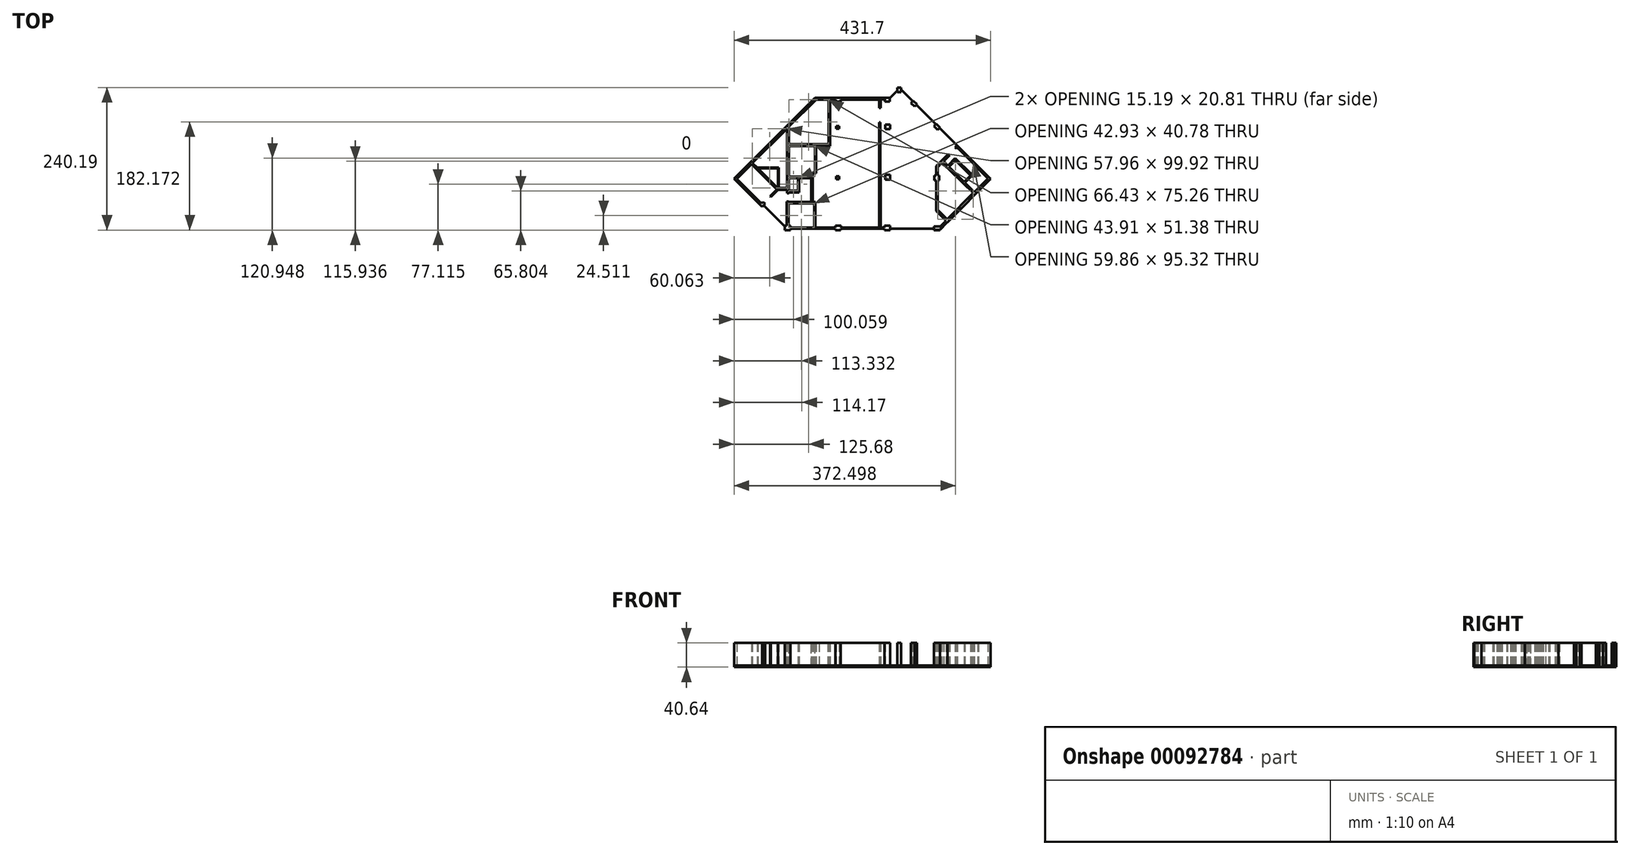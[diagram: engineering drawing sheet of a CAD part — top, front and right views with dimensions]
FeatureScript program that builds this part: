
annotation { "Feature Type Name" : "Feature", "Feature Type Description" : "" }
export const myFeature = defineFeature(function(context is Context, id is Id, definition is map)
    precondition{}
    {
        {
            var Q0;
            Q0=qCreatedBy(makeId("Top.planeOp"),FACE);
            var sketch = newSketch(context, id + "F0", { "sketchPlane" : qUnion([Q0])});
            skLineSegment(sketch, "E0", {"start": v(-79.76, 102.69) * mm, "end": v(-215.75, -33.59) * mm});
            skLineSegment(sketch, "E1", {"start": v(-215.75, -33.59) * mm, "end": v(-168.57, -80.77) * mm});
            skLineSegment(sketch, "E2", {"start": v(-168.57, -80.77) * mm, "end": v(-163.72, -75.92) * mm});
            skLineSegment(sketch, "E3", {"start": v(-163.72, -75.92) * mm, "end": v(-167.29, -72.36) * mm});
            skLineSegment(sketch, "E4", {"start": v(-167.29, -72.36) * mm, "end": v(-169.85, -74.93) * mm});
            skLineSegment(sketch, "E5", {"start": v(-169.85, -74.93) * mm, "end": v(-211.2, -33.59) * mm});
            skLineSegment(sketch, "E6", {"start": v(-211.2, -33.59) * mm, "end": v(-186.4, -8.8) * mm});
            skLineSegment(sketch, "E7", {"start": v(-186.4, -8.8) * mm, "end": v(-143.7, -51.47) * mm});
            skLineSegment(sketch, "E8", {"start": v(-143.7, -51.47) * mm, "end": v(-155.43, -62.87) * mm});
            skLineSegment(sketch, "E9", {"start": v(-155.43, -62.87) * mm, "end": v(-153.86, -64.43) * mm});
            skLineSegment(sketch, "E10", {"start": v(-153.86, -64.43) * mm, "end": v(-141.88, -52.4) * mm});
            skLineSegment(sketch, "E11", {"start": v(-141.88, -52.4) * mm, "end": v(-126.8, -52.4) * mm});
            skLineSegment(sketch, "E12", {"start": v(-126.8, -52.4) * mm, "end": v(-126.8, -58.13) * mm});
            skLineSegment(sketch, "E13", {"start": v(-126.8, -58.13) * mm, "end": v(-123.38, -58.13) * mm});
            skLineSegment(sketch, "E14", {"start": v(-123.38, -58.13) * mm, "end": v(-123.38, -56.96) * mm});
            skLineSegment(sketch, "E15", {"start": v(-123.38, -56.96) * mm, "end": v(-106.13, -56.96) * mm});
            skLineSegment(sketch, "E16", {"start": v(-106.13, -56.96) * mm, "end": v(-106.13, -50.83) * mm});
            skLineSegment(sketch, "E17", {"start": v(-106.13, -50.83) * mm, "end": v(-106.13, -40.44) * mm});
            skLineSegment(sketch, "E18", {"start": v(-106.13, -40.44) * mm, "end": v(-106.13, -32.6) * mm});
            skLineSegment(sketch, "E19", {"start": v(-106.13, -32.6) * mm, "end": v(-104.14, -32.6) * mm});
            skLineSegment(sketch, "E20", {"start": v(-104.14, -32.6) * mm, "end": v(-86.11, -32.44) * mm});
            skLineSegment(sketch, "E21", {"start": v(-86.11, -32.44) * mm, "end": v(-86.08, -56.63) * mm});
            skLineSegment(sketch, "E22", {"start": v(-86.08, -56.63) * mm, "end": v(-86.18, -72.93) * mm});
            skLineSegment(sketch, "E23", {"start": v(-86.18, -72.93) * mm, "end": v(-123.98, -72.93) * mm});
            skLineSegment(sketch, "E24", {"start": v(-123.98, -72.93) * mm, "end": v(-123.98, -71.84) * mm});
            skLineSegment(sketch, "E25", {"start": v(-123.98, -71.84) * mm, "end": v(-127, -71.84) * mm});
            skLineSegment(sketch, "E26", {"start": v(-127, -71.84) * mm, "end": v(-127, -112.56) * mm});
            skLineSegment(sketch, "E27", {"start": v(-127, -112.56) * mm, "end": v(-130.71, -112.56) * mm});
            skLineSegment(sketch, "E28", {"start": v(-130.71, -112.56) * mm, "end": v(-130.71, -120.1) * mm});
            skLineSegment(sketch, "E29", {"start": v(-130.71, -120.1) * mm, "end": v(-121.24, -120.1) * mm});
            skLineSegment(sketch, "E30", {"start": v(-121.24, -120.1) * mm, "end": v(-121.24, -117.8) * mm});
            skLineSegment(sketch, "E31", {"start": v(-121.24, -117.8) * mm, "end": v(-45.65, -117.8) * mm});
            skLineSegment(sketch, "E32", {"start": v(-45.65, -117.8) * mm, "end": v(-45.65, -120.1) * mm});
            skLineSegment(sketch, "E33", {"start": v(-45.65, -120.1) * mm, "end": v(-36.17, -120.1) * mm});
            skLineSegment(sketch, "E34", {"start": v(-36.17, -120.1) * mm, "end": v(-36.17, -117.8) * mm});
            skLineSegment(sketch, "E35", {"start": v(-36.17, -117.8) * mm, "end": v(30.57, -117.8) * mm});
            skLineSegment(sketch, "E36", {"start": v(30.57, -117.8) * mm, "end": v(30.57, -117.83) * mm});
            skLineSegment(sketch, "E37", {"start": v(30.57, -117.83) * mm, "end": v(37.4, -117.82) * mm});
            skLineSegment(sketch, "E38", {"start": v(37.4, -117.82) * mm, "end": v(37.4, -120.1) * mm});
            skLineSegment(sketch, "E39", {"start": v(37.4, -120.1) * mm, "end": v(46.88, -120.1) * mm});
            skLineSegment(sketch, "E40", {"start": v(46.88, -120.1) * mm, "end": v(46.88, -112.56) * mm});
            skLineSegment(sketch, "E41", {"start": v(46.88, -112.56) * mm, "end": v(37.4, -112.56) * mm});
            skLineSegment(sketch, "E42", {"start": v(37.4, -112.56) * mm, "end": v(37.4, -115.98) * mm});
            skLineSegment(sketch, "E43", {"start": v(37.4, -115.98) * mm, "end": v(30.64, -115.98) * mm});
            skLineSegment(sketch, "E44", {"start": v(30.64, -115.98) * mm, "end": v(30.28, 61.63) * mm});
            skLineSegment(sketch, "E45", {"start": v(30.28, 61.63) * mm, "end": v(28, 61.63) * mm});
            skLineSegment(sketch, "E46", {"start": v(28, 61.63) * mm, "end": v(28, -115.99) * mm});
            skLineSegment(sketch, "E47", {"start": v(28, -115.99) * mm, "end": v(-36.17, -115.99) * mm});
            skLineSegment(sketch, "E48", {"start": v(-36.17, -115.99) * mm, "end": v(-36.17, -112.56) * mm});
            skLineSegment(sketch, "E49", {"start": v(-36.17, -112.56) * mm, "end": v(-45.65, -112.56) * mm});
            skLineSegment(sketch, "E50", {"start": v(-45.65, -112.56) * mm, "end": v(-45.65, -115.99) * mm});
            skLineSegment(sketch, "E51", {"start": v(-45.65, -115.99) * mm, "end": v(-78.77, -115.99) * mm});
            skLineSegment(sketch, "E52", {"start": v(-78.77, -115.99) * mm, "end": v(-78.77, -72.93) * mm});
            skLineSegment(sketch, "E53", {"start": v(-78.77, -72.93) * mm, "end": v(-83.56, -72.93) * mm});
            skLineSegment(sketch, "E54", {"start": v(-83.56, -72.93) * mm, "end": v(-83.56, -58.24) * mm});
            skLineSegment(sketch, "E55", {"start": v(-83.56, -58.24) * mm, "end": v(-83.56, -24.67) * mm});
            skLineSegment(sketch, "E56", {"start": v(-83.56, -24.67) * mm, "end": v(-77.61, -24.67) * mm});
            skLineSegment(sketch, "E57", {"start": v(-77.61, -24.67) * mm, "end": v(-77.61, 21.4) * mm});
            skLineSegment(sketch, "E58", {"start": v(-77.61, 21.4) * mm, "end": v(-59.24, 21.44) * mm});
            skLineSegment(sketch, "E59", {"start": v(-59.24, 21.44) * mm, "end": v(-54.1, 21.44) * mm});
            skLineSegment(sketch, "E60", {"start": v(-54.1, 21.44) * mm, "end": v(-54.1, 99.7) * mm});
            skLineSegment(sketch, "E61", {"start": v(-54.1, 99.7) * mm, "end": v(-44.98, 99.7) * mm});
            skLineSegment(sketch, "E62", {"start": v(-44.98, 99.7) * mm, "end": v(-44.98, 96.56) * mm});
            skLineSegment(sketch, "E63", {"start": v(-44.98, 96.56) * mm, "end": v(-36.57, 96.56) * mm});
            skLineSegment(sketch, "E64", {"start": v(-36.57, 96.56) * mm, "end": v(-36.57, 99.7) * mm});
            skLineSegment(sketch, "E65", {"start": v(-36.57, 99.7) * mm, "end": v(28.57, 99.7) * mm});
            skLineSegment(sketch, "E66", {"start": v(28.57, 99.7) * mm, "end": v(28.57, 85.58) * mm});
            skLineSegment(sketch, "E67", {"start": v(28.57, 85.58) * mm, "end": v(30.91, 85.64) * mm});
            skLineSegment(sketch, "E68", {"start": v(30.91, 85.64) * mm, "end": v(30.91, 100.4) * mm});
            skLineSegment(sketch, "E69", {"start": v(30.91, 100.4) * mm, "end": v(37.7, 100.4) * mm});
            skLineSegment(sketch, "E70", {"start": v(37.7, 100.4) * mm, "end": v(37.7, 96.56) * mm});
            skLineSegment(sketch, "E71", {"start": v(37.7, 96.56) * mm, "end": v(46.1, 96.56) * mm});
            skLineSegment(sketch, "E72", {"start": v(46.1, 96.56) * mm, "end": v(46.1, 102.4) * mm});
            skLineSegment(sketch, "E73", {"start": v(46.1, 102.4) * mm, "end": v(37.73, 102.4) * mm});
            skLineSegment(sketch, "E74", {"start": v(37.73, 102.4) * mm, "end": v(37.7, 102.69) * mm});
            skLineSegment(sketch, "E75", {"start": v(37.7, 102.69) * mm, "end": v(-79.76, 102.69) * mm});
            skLineSegment(sketch, "E76", {"start": v(-77.91, 99.7) * mm, "end": v(-56.96, 99.7) * mm});
            skLineSegment(sketch, "E77", {"start": v(-56.96, 99.7) * mm, "end": v(-56.96, 24.5) * mm});
            skLineSegment(sketch, "E78", {"start": v(-56.96, 24.5) * mm, "end": v(-58.2, 24.43) * mm});
            skLineSegment(sketch, "E79", {"start": v(-58.2, 24.43) * mm, "end": v(-72.92, 24.58) * mm});
            skLineSegment(sketch, "E80", {"start": v(-72.92, 24.58) * mm, "end": v(-123.38, 24.47) * mm});
            skLineSegment(sketch, "E81", {"start": v(-123.38, 24.47) * mm, "end": v(-123.38, 54.22) * mm});
            skLineSegment(sketch, "E82", {"start": v(-123.38, 54.22) * mm, "end": v(-77.91, 99.7) * mm});
            skFitSpline(sketch, "E83", {"points": [v(-79.84, 21.43) * mm, v(-80.03, 20.07) * mm, v(-79.83, -23.46) * mm, v(-79.83, -23.46) * mm, v(-79.84, 21.43) * mm]});
            skLineSegment(sketch, "E84", {"start": v(-126.8, 50.8) * mm, "end": v(-126.8, -49.12) * mm});
            skLineSegment(sketch, "E85", {"start": v(-126.8, -49.12) * mm, "end": v(-140.51, -49.12) * mm});
            skLineSegment(sketch, "E86", {"start": v(-140.51, -49.12) * mm, "end": v(-140.51, -14.9) * mm});
            skLineSegment(sketch, "E87", {"start": v(-140.51, -14.9) * mm, "end": v(-177.03, -14.9) * mm});
            skLineSegment(sketch, "E88", {"start": v(-177.03, -14.9) * mm, "end": v(-184.77, -7.17) * mm});
            skLineSegment(sketch, "E89", {"start": v(-184.77, -7.17) * mm, "end": v(-126.8, 50.8) * mm});
            skLineSegment(sketch, "E90", {"start": v(-79.83, -23.46) * mm, "end": v(-85.98, -23.46) * mm});
            skLineSegment(sketch, "E91", {"start": v(-85.98, -23.46) * mm, "end": v(-85.98, -29.82) * mm});
            skLineSegment(sketch, "E92", {"start": v(-85.98, -29.82) * mm, "end": v(-88.67, -29.8) * mm});
            skLineSegment(sketch, "E93", {"start": v(-88.67, -29.8) * mm, "end": v(-93, -29.84) * mm});
            skLineSegment(sketch, "E94", {"start": v(-93, -29.84) * mm, "end": v(-100.1, -29.88) * mm});
            skLineSegment(sketch, "E95", {"start": v(-100.1, -29.88) * mm, "end": v(-103.14, -29.88) * mm});
            skLineSegment(sketch, "E96", {"start": v(-103.14, -29.88) * mm, "end": v(-123.38, -29.88) * mm});
            skLineSegment(sketch, "E97", {"start": v(-123.38, -29.88) * mm, "end": v(-123.38, 21.34) * mm});
            skLineSegment(sketch, "E98", {"start": v(-123.38, 21.34) * mm, "end": v(-79.84, 21.43) * mm});
            skLineSegment(sketch, "E99", {"start": v(-175.82, -16.1) * mm, "end": v(-141.82, -16.1) * mm});
            skLineSegment(sketch, "E100", {"start": v(-141.82, -16.1) * mm, "end": v(-141.82, -49.12) * mm});
            skLineSegment(sketch, "E101", {"start": v(-141.82, -49.12) * mm, "end": v(-142.77, -49.12) * mm});
            skLineSegment(sketch, "E102", {"start": v(-142.77, -49.12) * mm, "end": v(-175.82, -16.1) * mm});
            skLineSegment(sketch, "E103", {"start": v(-123.38, -32.6) * mm, "end": v(-108.2, -32.6) * mm});
            skLineSegment(sketch, "E104", {"start": v(-108.2, -32.6) * mm, "end": v(-108.2, -39.52) * mm});
            skLineSegment(sketch, "E105", {"start": v(-108.2, -39.52) * mm, "end": v(-108.4, -50.63) * mm});
            skLineSegment(sketch, "E106", {"start": v(-108.4, -50.63) * mm, "end": v(-108.38, -53.4) * mm});
            skLineSegment(sketch, "E107", {"start": v(-108.38, -53.4) * mm, "end": v(-123.38, -53.4) * mm});
            skLineSegment(sketch, "E108", {"start": v(-123.38, -53.4) * mm, "end": v(-123.38, -32.6) * mm});
            skLineSegment(sketch, "E109", {"start": v(-123.98, -75.2) * mm, "end": v(-81.05, -75.2) * mm});
            skLineSegment(sketch, "E110", {"start": v(-81.05, -75.2) * mm, "end": v(-81.05, -115.98) * mm});
            skLineSegment(sketch, "E111", {"start": v(-81.05, -115.98) * mm, "end": v(-121.24, -115.99) * mm});
            skLineSegment(sketch, "E112", {"start": v(-121.24, -115.99) * mm, "end": v(-121.24, -112.56) * mm});
            skLineSegment(sketch, "E113", {"start": v(-121.24, -112.56) * mm, "end": v(-123.98, -112.56) * mm});
            skLineSegment(sketch, "E114", {"start": v(-123.98, -112.56) * mm, "end": v(-123.98, -75.2) * mm});
            skLineSegment(sketch, "E115", {"start": v(-44.13, -29.6) * mm, "end": v(-39.28, -29.6) * mm});
            skLineSegment(sketch, "E116", {"start": v(-39.28, -29.6) * mm, "end": v(-39.28, -34.44) * mm});
            skLineSegment(sketch, "E117", {"start": v(-39.28, -34.44) * mm, "end": v(-44.13, -34.44) * mm});
            skLineSegment(sketch, "E118", {"start": v(-44.13, -34.44) * mm, "end": v(-44.13, -29.6) * mm});
            skLineSegment(sketch, "E119", {"start": v(-44.13, 55.22) * mm, "end": v(-39.28, 55.22) * mm});
            skLineSegment(sketch, "E120", {"start": v(-39.28, 55.22) * mm, "end": v(-39.28, 50.37) * mm});
            skLineSegment(sketch, "E121", {"start": v(-39.28, 50.37) * mm, "end": v(-44.13, 50.37) * mm});
            skLineSegment(sketch, "E122", {"start": v(-44.13, 50.37) * mm, "end": v(-44.13, 55.22) * mm});
            skLineSegment(sketch, "E123", {"start": v(124.21, -12.5) * mm, "end": v(124.21, -28.1) * mm});
            skLineSegment(sketch, "E124", {"start": v(124.21, -28.1) * mm, "end": v(121.15, -28.1) * mm});
            skLineSegment(sketch, "E125", {"start": v(121.15, -28.1) * mm, "end": v(121.15, -36.16) * mm});
            skLineSegment(sketch, "E126", {"start": v(121.15, -36.16) * mm, "end": v(124.21, -36.16) * mm});
            skLineSegment(sketch, "E127", {"start": v(124.21, -36.16) * mm, "end": v(124.21, -87.9) * mm});
            skLineSegment(sketch, "E128", {"start": v(124.21, -87.9) * mm, "end": v(140.84, -104.52) * mm});
            skLineSegment(sketch, "E129", {"start": v(140.84, -104.52) * mm, "end": v(130.48, -114.68) * mm});
            skLineSegment(sketch, "E130", {"start": v(130.48, -114.68) * mm, "end": v(130.48, -113.87) * mm});
            skLineSegment(sketch, "E131", {"start": v(130.48, -113.87) * mm, "end": v(120.5, -113.87) * mm});
            skLineSegment(sketch, "E132", {"start": v(120.5, -113.87) * mm, "end": v(120.5, -119.86) * mm});
            skLineSegment(sketch, "E133", {"start": v(120.5, -119.86) * mm, "end": v(130.48, -119.86) * mm});
            skLineSegment(sketch, "E134", {"start": v(130.48, -119.86) * mm, "end": v(130.48, -119.2) * mm});
            skLineSegment(sketch, "E135", {"start": v(130.48, -119.2) * mm, "end": v(143.25, -106.64) * mm});
            skLineSegment(sketch, "E136", {"start": v(143.25, -106.64) * mm, "end": v(143.23, -106.61) * mm});
            skLineSegment(sketch, "E137", {"start": v(143.23, -106.61) * mm, "end": v(215.8, -34.05) * mm});
            skLineSegment(sketch, "E138", {"start": v(215.8, -34.05) * mm, "end": v(159.12, 22.67) * mm});
            skLineSegment(sketch, "E139", {"start": v(159.12, 22.67) * mm, "end": v(155.8, 19.35) * mm});
            skLineSegment(sketch, "E140", {"start": v(155.8, 19.35) * mm, "end": v(157.97, 16.96) * mm});
            skLineSegment(sketch, "E141", {"start": v(157.97, 16.96) * mm, "end": v(159.6, 18.6) * mm});
            skLineSegment(sketch, "E142", {"start": v(159.6, 18.6) * mm, "end": v(193.9, -15.7) * mm});
            skLineSegment(sketch, "E143", {"start": v(193.9, -15.7) * mm, "end": v(183.71, -26.47) * mm});
            skLineSegment(sketch, "E144", {"start": v(183.71, -26.47) * mm, "end": v(156.22, 0.98) * mm});
            skLineSegment(sketch, "E145", {"start": v(156.22, 0.98) * mm, "end": v(144, -11.5) * mm});
            skLineSegment(sketch, "E146", {"start": v(144, -11.5) * mm, "end": v(136.9, -4.05) * mm});
            skLineSegment(sketch, "E147", {"start": v(136.9, -4.05) * mm, "end": v(147, 5.96) * mm});
            skLineSegment(sketch, "E148", {"start": v(147, 5.96) * mm, "end": v(144.77, 8.15) * mm});
            skLineSegment(sketch, "E149", {"start": v(144.77, 8.15) * mm, "end": v(131.84, -4.77) * mm});
            skLineSegment(sketch, "E150", {"start": v(131.84, -4.77) * mm, "end": v(124.21, -12.5) * mm});
            skLineSegment(sketch, "E151", {"start": v(186.58, -57.67) * mm, "end": v(142.79, -101.97) * mm});
            skLineSegment(sketch, "E152", {"start": v(142.79, -101.97) * mm, "end": v(126.72, -85.9) * mm});
            skLineSegment(sketch, "E153", {"start": v(126.72, -85.9) * mm, "end": v(126.72, -36.16) * mm});
            skLineSegment(sketch, "E154", {"start": v(126.72, -36.16) * mm, "end": v(129.21, -36.16) * mm});
            skLineSegment(sketch, "E155", {"start": v(129.21, -36.16) * mm, "end": v(129.21, -28.1) * mm});
            skLineSegment(sketch, "E156", {"start": v(129.21, -28.1) * mm, "end": v(126.72, -28.1) * mm});
            skLineSegment(sketch, "E157", {"start": v(126.72, -28.1) * mm, "end": v(126.72, -14) * mm});
            skLineSegment(sketch, "E158", {"start": v(126.72, -14) * mm, "end": v(133.83, -6.64) * mm});
            skLineSegment(sketch, "E159", {"start": v(133.83, -6.64) * mm, "end": v(186.58, -57.67) * mm});
            skLineSegment(sketch, "E160", {"start": v(156.57, -2.8) * mm, "end": v(182.11, -28.33) * mm});
            skLineSegment(sketch, "E161", {"start": v(182.11, -28.33) * mm, "end": v(171.2, -38.85) * mm});
            skLineSegment(sketch, "E162", {"start": v(171.2, -38.85) * mm, "end": v(145.9, -13.47) * mm});
            skLineSegment(sketch, "E163", {"start": v(145.9, -13.47) * mm, "end": v(156.57, -2.8) * mm});
            skLineSegment(sketch, "E164", {"start": v(195.4, -17.25) * mm, "end": v(211.45, -33.3) * mm});
            skLineSegment(sketch, "E165", {"start": v(211.45, -33.3) * mm, "end": v(188.53, -56.22) * mm});
            skLineSegment(sketch, "E166", {"start": v(188.53, -56.22) * mm, "end": v(172.68, -40.32) * mm});
            skLineSegment(sketch, "E167", {"start": v(172.68, -40.32) * mm, "end": v(195.4, -17.25) * mm});
            skLineSegment(sketch, "E168", {"start": v(38.5, 57.78) * mm, "end": v(46.56, 57.78) * mm});
            skLineSegment(sketch, "E169", {"start": v(46.56, 57.78) * mm, "end": v(46.56, 49.71) * mm});
            skLineSegment(sketch, "E170", {"start": v(46.56, 49.71) * mm, "end": v(38.5, 49.71) * mm});
            skLineSegment(sketch, "E171", {"start": v(38.5, 49.71) * mm, "end": v(38.5, 57.78) * mm});
            skLineSegment(sketch, "E172", {"start": v(38.5, -26.89) * mm, "end": v(46.56, -26.89) * mm});
            skLineSegment(sketch, "E173", {"start": v(46.56, -26.89) * mm, "end": v(46.56, -34.95) * mm});
            skLineSegment(sketch, "E174", {"start": v(46.56, -34.95) * mm, "end": v(38.5, -34.95) * mm});
            skLineSegment(sketch, "E175", {"start": v(38.5, -34.95) * mm, "end": v(38.5, -26.89) * mm});
            skLineSegment(sketch, "E176", {"start": v(124.36, 58.9) * mm, "end": v(130.49, 52.76) * mm});
            skLineSegment(sketch, "E177", {"start": v(130.49, 52.76) * mm, "end": v(126.7, 48.97) * mm});
            skLineSegment(sketch, "E178", {"start": v(126.7, 48.97) * mm, "end": v(120.57, 55.1) * mm});
            skLineSegment(sketch, "E179", {"start": v(120.57, 55.1) * mm, "end": v(124.36, 58.9) * mm});
            skLineSegment(sketch, "E180", {"start": v(85.58, 97.67) * mm, "end": v(91.72, 91.54) * mm});
            skLineSegment(sketch, "E181", {"start": v(91.72, 91.54) * mm, "end": v(87.93, 87.75) * mm});
            skLineSegment(sketch, "E182", {"start": v(87.93, 87.75) * mm, "end": v(81.8, 93.88) * mm});
            skLineSegment(sketch, "E183", {"start": v(81.8, 93.88) * mm, "end": v(85.58, 97.67) * mm});
            skLineSegment(sketch, "E184", {"start": v(58.79, 120.08) * mm, "end": v(65.06, 120.08) * mm});
            skLineSegment(sketch, "E185", {"start": v(65.06, 120.08) * mm, "end": v(65.06, 112.38) * mm});
            skLineSegment(sketch, "E186", {"start": v(65.06, 112.38) * mm, "end": v(58.79, 112.38) * mm});
            skLineSegment(sketch, "E187", {"start": v(58.79, 112.38) * mm, "end": v(58.79, 120.08) * mm});
            skLineSegment(sketch, "E188", {"start": v(-215.85, -33.54) * mm, "end": v(-79.78, 102.73) * mm});
            skLineSegment(sketch, "E189", {"start": v(-79.78, 102.73) * mm, "end": v(46.96, 102.73) * mm});
            skLineSegment(sketch, "E190", {"start": v(46.96, 102.73) * mm, "end": v(58.85, 114.63) * mm});
            skLineSegment(sketch, "E191", {"start": v(58.85, 114.63) * mm, "end": v(58.85, 120.11) * mm});
            skLineSegment(sketch, "E192", {"start": v(58.85, 120.11) * mm, "end": v(65.02, 120.11) * mm});
            skLineSegment(sketch, "E193", {"start": v(65.02, 120.11) * mm, "end": v(65.02, 116.65) * mm});
            skLineSegment(sketch, "E194", {"start": v(65.02, 116.65) * mm, "end": v(84.8, 96.88) * mm});
            skLineSegment(sketch, "E195", {"start": v(84.8, 96.88) * mm, "end": v(85.59, 97.66) * mm});
            skLineSegment(sketch, "E196", {"start": v(85.59, 97.66) * mm, "end": v(91.7, 91.55) * mm});
            skLineSegment(sketch, "E197", {"start": v(91.7, 91.55) * mm, "end": v(90.95, 90.8) * mm});
            skLineSegment(sketch, "E198", {"start": v(90.95, 90.8) * mm, "end": v(123.63, 58.12) * mm});
            skLineSegment(sketch, "E199", {"start": v(123.63, 58.12) * mm, "end": v(124.34, 58.83) * mm});
            skLineSegment(sketch, "E200", {"start": v(124.34, 58.83) * mm, "end": v(130.43, 52.74) * mm});
            skLineSegment(sketch, "E201", {"start": v(130.43, 52.74) * mm, "end": v(129.76, 52.06) * mm});
            skLineSegment(sketch, "E202", {"start": v(129.76, 52.06) * mm, "end": v(215.85, -34.03) * mm});
            skLineSegment(sketch, "E203", {"start": v(215.85, -34.03) * mm, "end": v(130.5, -119.38) * mm});
            skLineSegment(sketch, "E204", {"start": v(130.5, -119.38) * mm, "end": v(130.5, -119.93) * mm});
            skLineSegment(sketch, "E205", {"start": v(130.5, -119.93) * mm, "end": v(120.44, -119.93) * mm});
            skLineSegment(sketch, "E206", {"start": v(120.44, -119.93) * mm, "end": v(120.44, -117.62) * mm});
            skLineSegment(sketch, "E207", {"start": v(120.44, -117.62) * mm, "end": v(46.89, -117.62) * mm});
            skLineSegment(sketch, "E208", {"start": v(46.89, -117.62) * mm, "end": v(46.89, -120.08) * mm});
            skLineSegment(sketch, "E209", {"start": v(46.89, -120.08) * mm, "end": v(37.4, -120.08) * mm});
            skLineSegment(sketch, "E210", {"start": v(37.4, -120.08) * mm, "end": v(37.4, -117.8) * mm});
            skLineSegment(sketch, "E211", {"start": v(37.4, -117.8) * mm, "end": v(-36.22, -117.8) * mm});
            skLineSegment(sketch, "E212", {"start": v(-36.22, -117.8) * mm, "end": v(-36.22, -120.08) * mm});
            skLineSegment(sketch, "E213", {"start": v(-36.22, -120.08) * mm, "end": v(-45.66, -120.08) * mm});
            skLineSegment(sketch, "E214", {"start": v(-45.66, -120.08) * mm, "end": v(-45.66, -117.76) * mm});
            skLineSegment(sketch, "E215", {"start": v(-45.66, -117.76) * mm, "end": v(-121.24, -117.76) * mm});
            skLineSegment(sketch, "E216", {"start": v(-121.24, -117.76) * mm, "end": v(-121.24, -120.11) * mm});
            skLineSegment(sketch, "E217", {"start": v(-121.24, -120.11) * mm, "end": v(-130.72, -120.11) * mm});
            skLineSegment(sketch, "E218", {"start": v(-130.72, -120.11) * mm, "end": v(-130.72, -114.02) * mm});
            skLineSegment(sketch, "E219", {"start": v(-130.72, -114.02) * mm, "end": v(-166.3, -78.46) * mm});
            skLineSegment(sketch, "E220", {"start": v(-166.3, -78.46) * mm, "end": v(-168.6, -80.76) * mm});
            skLineSegment(sketch, "E221", {"start": v(-168.6, -80.76) * mm, "end": v(-215.85, -33.54) * mm});
            skSolve(sketch);
        }
        {
            var Q0;
            {var subQ13=sQuery(id+"F0.wireOp",EDGE,"E0");Q0=makeQuery(id+"F0.imprint","IMPRINT",FACE,{"disambiguationData":[TD([[makeQuery(id+"F0.imprint","IMPRINT",EDGE,{"derivedFrom":subQ13}),1.0]])]});}
            var Q1;
            Q1=makeQuery(id+"F0.imprint","IMPRINT",FACE,{"disambiguationData":[TD([[makeQuery(id+"F0.imprint","IMPRINT",EDGE,{"derivedFrom":sQuery(id+"F0.wireOp",EDGE,"E168")}),-1.0]])]});
            var Q2;
            Q2=makeQuery(id+"F0.imprint","IMPRINT",FACE,{"disambiguationData":[TD([[makeQuery(id+"F0.imprint","IMPRINT",EDGE,{"derivedFrom":sQuery(id+"F0.wireOp",EDGE,"E119")}),-1.0]])]});
            var Q3;
            Q3=makeQuery(id+"F0.imprint","IMPRINT",FACE,{"disambiguationData":[TD([[makeQuery(id+"F0.imprint","IMPRINT",EDGE,{"derivedFrom":sQuery(id+"F0.wireOp",EDGE,"E115")}),-1.0]])]});
            var Q4;
            Q4=makeQuery(id+"F0.imprint","IMPRINT",FACE,{"disambiguationData":[TD([[makeQuery(id+"F0.imprint","IMPRINT",EDGE,{"derivedFrom":sQuery(id+"F0.wireOp",EDGE,"E172")}),-1.0]])]});
            var Q5;
            Q5=makeQuery(id+"F0.imprint","IMPRINT",FACE,{"disambiguationData":[TD([[makeQuery(id+"F0.imprint","IMPRINT",EDGE,{"derivedFrom":sQuery(id+"F0.wireOp",EDGE,"E123")}),1.0]])]});
            var Q6;
            {var subQ4=sQuery(id+"F0.wireOp",EDGE,"E178");Q6=makeQuery(id+"F0.imprint","IMPRINT",FACE,{"disambiguationData":[TD([[makeQuery(id+"F0.imprint","IMPRINT",EDGE,{"derivedFrom":subQ4}),-1.0]])]});}
            var Q7;
            {var subQ4=sQuery(id+"F0.wireOp",EDGE,"E182");Q7=makeQuery(id+"F0.imprint","IMPRINT",FACE,{"disambiguationData":[TD([[makeQuery(id+"F0.imprint","IMPRINT",EDGE,{"derivedFrom":subQ4}),-1.0]])]});}
            var Q8;
            {var subQ1=sQuery(id+"F0.wireOp",EDGE,"E186");Q8=makeQuery(id+"F0.imprint","IMPRINT",FACE,{"disambiguationData":[TD([[makeQuery(id+"F0.imprint","IMPRINT",EDGE,{"derivedFrom":subQ1}),-1.0]])]});}
            extrude(context, id + "F1", {"entities" : qUnion([Q0, Q1, Q2, Q3, Q4, Q5, Q6, Q7, Q8]), "depth" : 40.64 * mm});
        }
        {
            var Q0;
            Q0=makeQuery(id+"F1.opExtrude","CAP_FACE",FACE,{"disambiguationData":[OSD([sQuery(id+"F0.wireOp",EDGE,"E0"),sQuery(id+"F0.wireOp",EDGE,"E1"),sQuery(id+"F0.wireOp",EDGE,"E2"),sQuery(id+"F0.wireOp",EDGE,"E3"),sQuery(id+"F0.wireOp",EDGE,"E4"),sQuery(id+"F0.wireOp",EDGE,"E5"),sQuery(id+"F0.wireOp",EDGE,"E6"),sQuery(id+"F0.wireOp",EDGE,"E7"),sQuery(id+"F0.wireOp",EDGE,"E8"),sQuery(id+"F0.wireOp",EDGE,"E9"),sQuery(id+"F0.wireOp",EDGE,"E10"),sQuery(id+"F0.wireOp",EDGE,"E11"),sQuery(id+"F0.wireOp",EDGE,"E12"),sQuery(id+"F0.wireOp",EDGE,"E13"),sQuery(id+"F0.wireOp",EDGE,"E14"),sQuery(id+"F0.wireOp",EDGE,"E15"),sQuery(id+"F0.wireOp",EDGE,"E16"),sQuery(id+"F0.wireOp",EDGE,"E17"),sQuery(id+"F0.wireOp",EDGE,"E18"),sQuery(id+"F0.wireOp",EDGE,"E19"),sQuery(id+"F0.wireOp",EDGE,"E20"),sQuery(id+"F0.wireOp",EDGE,"E21"),sQuery(id+"F0.wireOp",EDGE,"E22"),sQuery(id+"F0.wireOp",EDGE,"E23"),sQuery(id+"F0.wireOp",EDGE,"E24"),sQuery(id+"F0.wireOp",EDGE,"E25"),sQuery(id+"F0.wireOp",EDGE,"E26"),sQuery(id+"F0.wireOp",EDGE,"E27"),sQuery(id+"F0.wireOp",EDGE,"E28"),sQuery(id+"F0.wireOp",EDGE,"E29"),sQuery(id+"F0.wireOp",EDGE,"E31"),sQuery(id+"F0.wireOp",EDGE,"E32"),sQuery(id+"F0.wireOp",EDGE,"E40"),sQuery(id+"F0.wireOp",EDGE,"E41"),sQuery(id+"F0.wireOp",EDGE,"E42"),sQuery(id+"F0.wireOp",EDGE,"E43"),sQuery(id+"F0.wireOp",EDGE,"E44"),sQuery(id+"F0.wireOp",EDGE,"E45"),sQuery(id+"F0.wireOp",EDGE,"E46"),sQuery(id+"F0.wireOp",EDGE,"E47"),sQuery(id+"F0.wireOp",EDGE,"E48"),sQuery(id+"F0.wireOp",EDGE,"E49"),sQuery(id+"F0.wireOp",EDGE,"E50"),sQuery(id+"F0.wireOp",EDGE,"E51"),sQuery(id+"F0.wireOp",EDGE,"E52"),sQuery(id+"F0.wireOp",EDGE,"E53"),sQuery(id+"F0.wireOp",EDGE,"E54"),sQuery(id+"F0.wireOp",EDGE,"E55"),sQuery(id+"F0.wireOp",EDGE,"E56"),sQuery(id+"F0.wireOp",EDGE,"E57"),sQuery(id+"F0.wireOp",EDGE,"E58"),sQuery(id+"F0.wireOp",EDGE,"E59"),sQuery(id+"F0.wireOp",EDGE,"E60"),sQuery(id+"F0.wireOp",EDGE,"E61"),sQuery(id+"F0.wireOp",EDGE,"E62"),sQuery(id+"F0.wireOp",EDGE,"E63"),sQuery(id+"F0.wireOp",EDGE,"E64"),sQuery(id+"F0.wireOp",EDGE,"E65"),sQuery(id+"F0.wireOp",EDGE,"E66"),sQuery(id+"F0.wireOp",EDGE,"E67"),sQuery(id+"F0.wireOp",EDGE,"E68"),sQuery(id+"F0.wireOp",EDGE,"E69"),sQuery(id+"F0.wireOp",EDGE,"E70"),sQuery(id+"F0.wireOp",EDGE,"E71"),sQuery(id+"F0.wireOp",EDGE,"E72"),sQuery(id+"F0.wireOp",EDGE,"E73"),sQuery(id+"F0.wireOp",EDGE,"E74"),sQuery(id+"F0.wireOp",EDGE,"E75"),sQuery(id+"F0.wireOp",EDGE,"E76"),sQuery(id+"F0.wireOp",EDGE,"E77"),sQuery(id+"F0.wireOp",EDGE,"E78"),sQuery(id+"F0.wireOp",EDGE,"E79"),sQuery(id+"F0.wireOp",EDGE,"E80"),sQuery(id+"F0.wireOp",EDGE,"E81"),sQuery(id+"F0.wireOp",EDGE,"E82"),sQuery(id+"F0.wireOp",EDGE,"E84"),sQuery(id+"F0.wireOp",EDGE,"E85"),sQuery(id+"F0.wireOp",EDGE,"E86"),sQuery(id+"F0.wireOp",EDGE,"E87"),sQuery(id+"F0.wireOp",EDGE,"E88"),sQuery(id+"F0.wireOp",EDGE,"E89"),sQuery(id+"F0.wireOp",EDGE,"E99"),sQuery(id+"F0.wireOp",EDGE,"E100"),sQuery(id+"F0.wireOp",EDGE,"E101"),sQuery(id+"F0.wireOp",EDGE,"E102"),sQuery(id+"F0.wireOp",EDGE,"E103"),sQuery(id+"F0.wireOp",EDGE,"E104"),sQuery(id+"F0.wireOp",EDGE,"E105"),sQuery(id+"F0.wireOp",EDGE,"E106"),sQuery(id+"F0.wireOp",EDGE,"E107"),sQuery(id+"F0.wireOp",EDGE,"E108"),sQuery(id+"F0.wireOp",EDGE,"E109"),sQuery(id+"F0.wireOp",EDGE,"E110"),sQuery(id+"F0.wireOp",EDGE,"E111"),sQuery(id+"F0.wireOp",EDGE,"E112"),sQuery(id+"F0.wireOp",EDGE,"E113"),sQuery(id+"F0.wireOp",EDGE,"E114"),sQuery(id+"F0.wireOp",EDGE,"E209"),sQuery(id+"F0.wireOp",EDGE,"E210"),sQuery(id+"F0.wireOp",EDGE,"E211"),sQuery(id+"F0.wireOp",EDGE,"E212"),sQuery(id+"F0.wireOp",EDGE,"E213"),sQuery(id+"F0.wireOp",EDGE,"E214"),sQuery(id+"F0.wireOp",EDGE,"E215"),sQuery(id+"F0.wireOp",EDGE,"E216"),sQuery(id+"F0.wireOp",EDGE,"E219"),sQuery(id+"F0.wireOp",EDGE,"E220")])],"isStart":false});
            var sketch = newSketch(context, id + "F2", { "sketchPlane" : qUnion([Q0])});
            skLineSegment(sketch, "E222", {"start": v(-123.63, 21.52) * mm, "end": v(-79.73, 21.52) * mm});
            skLineSegment(sketch, "E223", {"start": v(-79.73, 21.52) * mm, "end": v(-79.73, -23.43) * mm});
            skLineSegment(sketch, "E224", {"start": v(-79.73, -23.43) * mm, "end": v(-86.14, -23.43) * mm});
            skLineSegment(sketch, "E225", {"start": v(-86.14, -23.43) * mm, "end": v(-86.14, -29.86) * mm});
            skLineSegment(sketch, "E226", {"start": v(-86.14, -29.86) * mm, "end": v(-123.62, -29.86) * mm});
            skLineSegment(sketch, "E227", {"start": v(-123.62, -29.86) * mm, "end": v(-123.63, 21.52) * mm});
            skSolve(sketch);
        }
        {
            var Q0;
            Q0=makeQuery(id+"F2.imprint","IMPRINT",FACE,{"disambiguationData":[TD([[makeQuery(id+"F2.imprint","IMPRINT",EDGE,{"derivedFrom":sQuery(id+"F2.wireOp",EDGE,"E222")}),-1.0]])]});
            extrude(context, id + "F3", {"entities" : qUnion([Q0]), "operationType" : NewBodyOperationType.REMOVE, "oppositeDirection" : true, "depth" : 40.64 * mm});
        }
        {
            var Q0;
            {var subQ23=sQuery(id+"F0.wireOp",EDGE,"E0");Q0=makeQuery(id+"F0.imprint","IMPRINT",FACE,{"disambiguationData":[TD([[makeQuery(id+"F0.imprint","IMPRINT",EDGE,{"derivedFrom":subQ23}),-1.0]])]});}
            var Q1;
            Q1=makeQuery(id+"F0.imprint","IMPRINT",FACE,{"disambiguationData":[TD([[makeQuery(id+"F0.imprint","IMPRINT",EDGE,{"derivedFrom":sQuery(id+"F0.wireOp",EDGE,"E76")}),-1.0]])]});
            var Q2;
            Q2=makeQuery(id+"F0.imprint","IMPRINT",FACE,{"disambiguationData":[TD([[makeQuery(id+"F0.imprint","IMPRINT",EDGE,{"derivedFrom":sQuery(id+"F0.wireOp",EDGE,"E84")}),-1.0]])]});
            var Q3;
            Q3=makeQuery(id+"F0.imprint","IMPRINT",FACE,{"disambiguationData":[TD([[makeQuery(id+"F0.imprint","IMPRINT",EDGE,{"derivedFrom":sQuery(id+"F0.wireOp",EDGE,"E99")}),-1.0]])]});
            var Q4;
            {var subQ5=sQuery(id+"F0.wireOp",EDGE,"E3");Q4=makeQuery(id+"F0.imprint","IMPRINT",FACE,{"disambiguationData":[TD([[makeQuery(id+"F0.imprint","IMPRINT",EDGE,{"derivedFrom":subQ5}),-1.0]])]});}
            var Q5;
            Q5=makeQuery(id+"F0.imprint","IMPRINT",FACE,{"disambiguationData":[TD([[makeQuery(id+"F0.imprint","IMPRINT",EDGE,{"derivedFrom":sQuery(id+"F0.wireOp",EDGE,"E109")}),-1.0]])]});
            var Q6;
            {var subQ13=sQuery(id+"F0.wireOp",EDGE,"E0");Q6=makeQuery(id+"F0.imprint","IMPRINT",FACE,{"disambiguationData":[TD([[makeQuery(id+"F0.imprint","IMPRINT",EDGE,{"derivedFrom":subQ13}),1.0]])]});}
            var Q7;
            Q7=makeQuery(id+"F0.imprint","IMPRINT",FACE,{"disambiguationData":[TD([[makeQuery(id+"F0.imprint","IMPRINT",EDGE,{"derivedFrom":sQuery(id+"F0.wireOp",EDGE,"E151")}),-1.0]])]});
            var Q8;
            Q8=makeQuery(id+"F0.imprint","IMPRINT",FACE,{"disambiguationData":[TD([[makeQuery(id+"F0.imprint","IMPRINT",EDGE,{"derivedFrom":sQuery(id+"F0.wireOp",EDGE,"E160")}),-1.0]])]});
            var Q9;
            Q9=makeQuery(id+"F0.imprint","IMPRINT",FACE,{"disambiguationData":[TD([[makeQuery(id+"F0.imprint","IMPRINT",EDGE,{"derivedFrom":sQuery(id+"F0.wireOp",EDGE,"E164")}),-1.0]])]});
            extrude(context, id + "F4", {"entities" : qUnion([Q0, Q1, Q2, Q3, Q4, Q5, Q6, Q7, Q8, Q9]), "depth" : 2.54 * mm});
        }
    });
